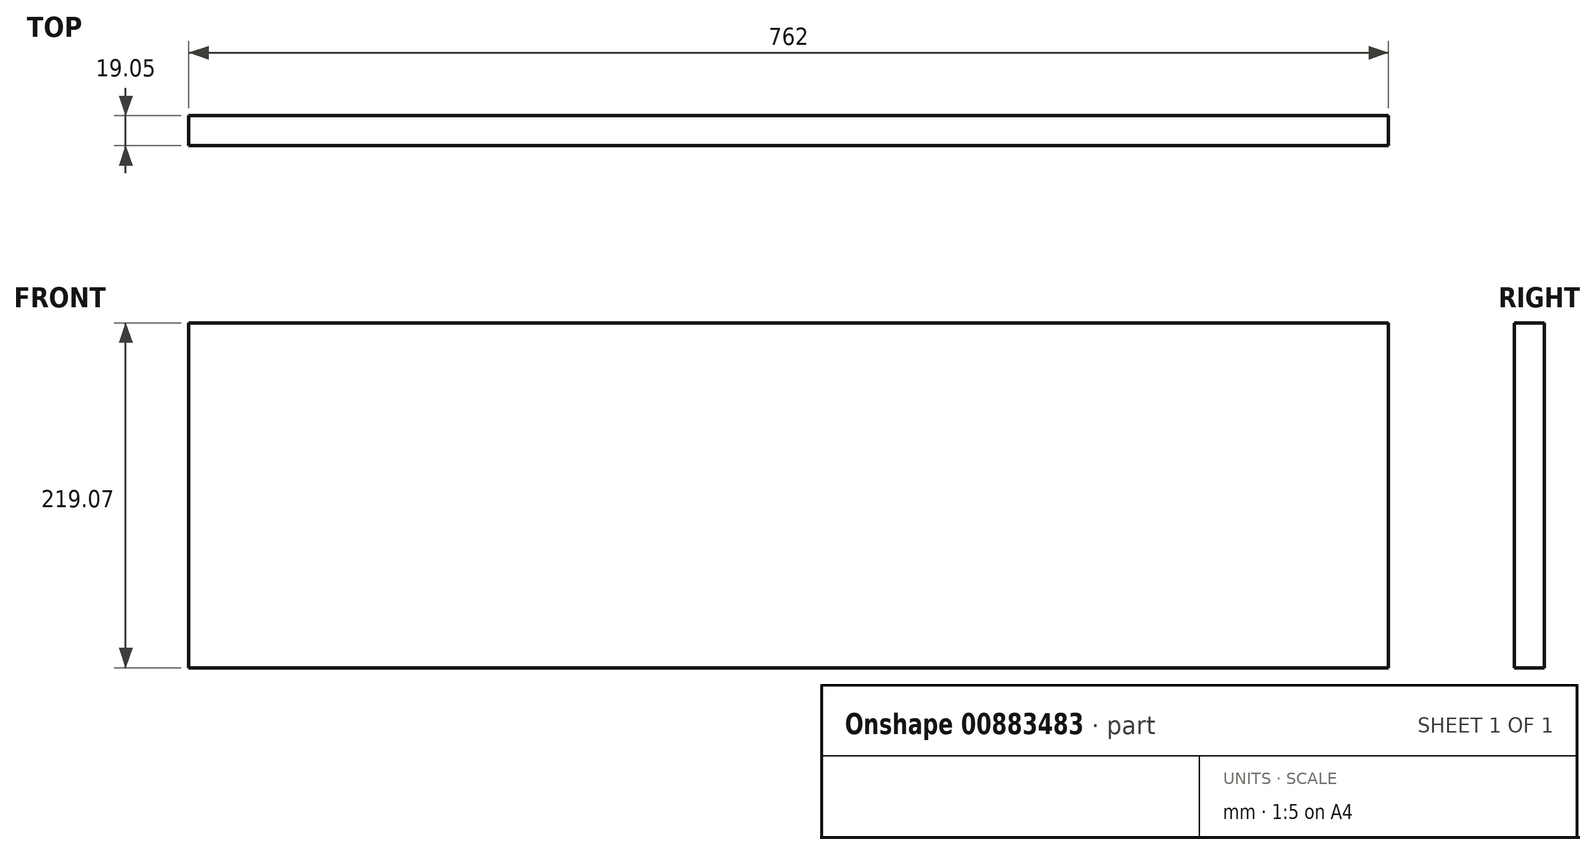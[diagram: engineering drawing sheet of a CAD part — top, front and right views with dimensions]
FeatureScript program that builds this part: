
annotation { "Feature Type Name" : "Feature", "Feature Type Description" : "" }
export const myFeature = defineFeature(function(context is Context, id is Id, definition is map)
    precondition{}
    {
        {
            var Q0;
            Q0=qCreatedBy(makeId("Front.planeOp"),FACE);
            var sketch = newSketch(context, id + "F0", { "sketchPlane" : qUnion([Q0])});
            skLineSegment(sketch, "E0.bottom", {"start": v(0, 0) * mm, "end": v(762, 0) * mm});
            skLineSegment(sketch, "E0.top", {"start": v(0, 219.07) * mm, "end": v(762, 219.07) * mm});
            skLineSegment(sketch, "E0.left", {"start": v(0, 0) * mm, "end": v(0, 219.07) * mm});
            skLineSegment(sketch, "E0.right", {"start": v(762, 0) * mm, "end": v(762, 219.07) * mm});
            skSolve(sketch);
        }
        {
            var Q0;
            Q0 = qSketchRegion(id + "F0", true);
            extrude(context, id + "F1", {"entities" : qUnion([Q0]), "depth" : 19.05 * mm, "offsetDistance" : 25.4 * mm});
        }
    });
